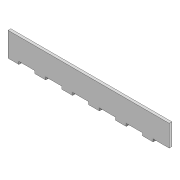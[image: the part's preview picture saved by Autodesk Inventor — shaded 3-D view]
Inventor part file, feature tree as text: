
AUTODESK INVENTOR PART (.ipt)
format: ipt  version: 2020 (Build 240168000, 168)  size: 116,736 bytes
history: native  units: mm
features: extrude x2, sketch x2
ambient origin geometry x8: Origin, YZ Plane, XZ Plane, XY Plane, X Axis, Y Axis, Z Axis, Center Point
bodies: Solid1 (feature_tree)
feature tree (4):
  extrude  "Base"  Depth=40.0mm
  extrude  "Encaixe"  Depth=20.0mm
  sketch  "Sketch1"  dims[d0=300.0mm d1=40.0mm]
  sketch  "Sketch2"  dims[d2=5.0mm d3=0.0mm d4=20.0mm d5=5.0mm d6=60.0mm d8=50.0mm d9=10.0mm d11=10.0mm d13=5.0mm d14=0.0mm]
